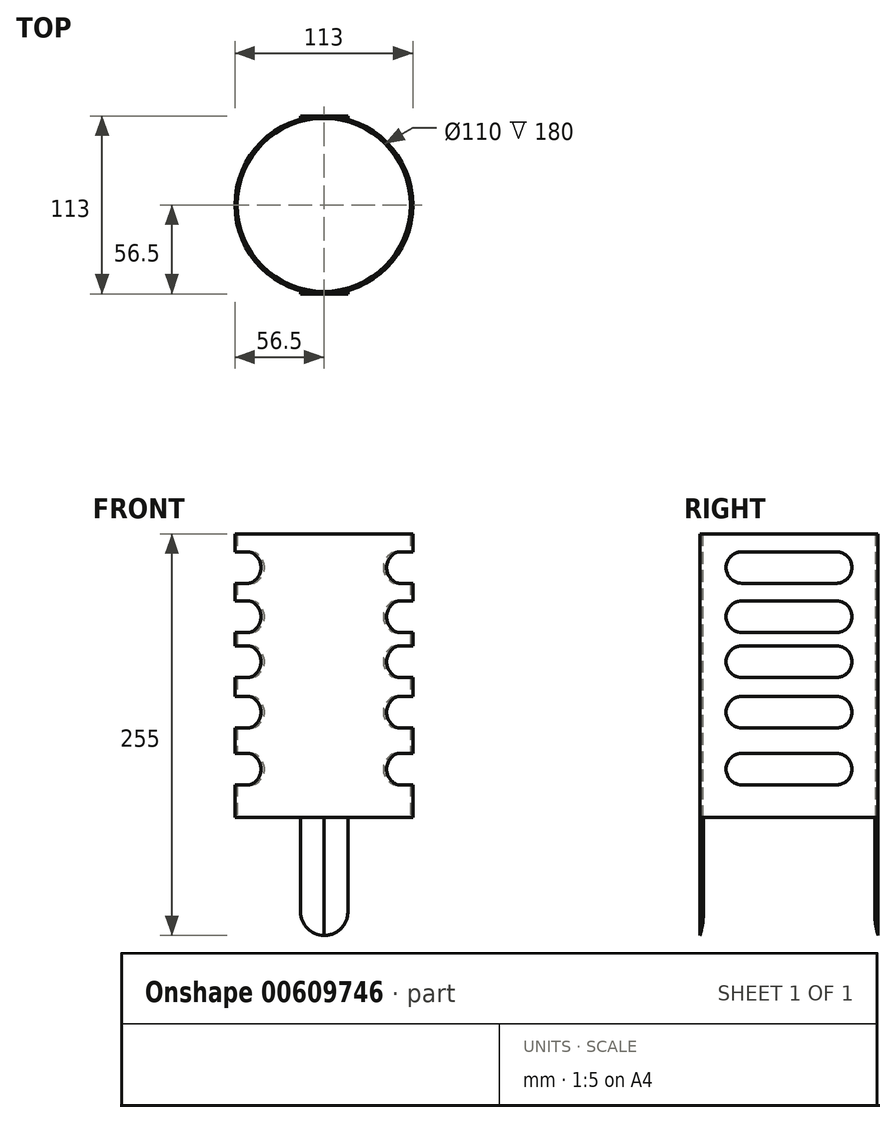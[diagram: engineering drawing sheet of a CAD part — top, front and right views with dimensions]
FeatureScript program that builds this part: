
annotation { "Feature Type Name" : "Feature", "Feature Type Description" : "" }
export const myFeature = defineFeature(function(context is Context, id is Id, definition is map)
    precondition{}
    {
        {
            var Q0;
            Q0=qCreatedBy(makeId("Top.planeOp"),FACE);
            var sketch = newSketch(context, id + "F0", { "sketchPlane" : qUnion([Q0])});
            skCircle(sketch, "E0", {"center": v(0, 0) * mm, "radius": 55 * mm});
            skCircle(sketch, "E1", {"center": v(0, 0) * mm, "radius": 56.5 * mm});
            skSolve(sketch);
        }
        {
            var Q0;
            Q0 = qSketchRegion(id + "F0", true);
            extrude(context, id + "F1", {"entities" : qUnion([Q0]), "depth" : 180 * mm, "offsetDistance" : 25 * mm});
        }
        {
            var Q0;
            Q0=qCreatedBy(makeId("Right.planeOp"),FACE);
            var sketch = newSketch(context, id + "F2", { "sketchPlane" : qUnion([Q0])});
            skLineSegment(sketch, "E2.bottom", {"start": v(-30, 20.7) * mm, "end": v(30, 20.7) * mm});
            skLineSegment(sketch, "E2.top", {"start": v(-30, 40.7) * mm, "end": v(30, 40.7) * mm});
            skLineSegment(sketch, "E2.left", {"start": v(-40, 30.7) * mm, "end": v(-40, 30.7) * mm});
            skLineSegment(sketch, "E2.right", {"start": v(40, 30.7) * mm, "end": v(40, 30.7) * mm});
            skLineSegment(sketch, "E3.bottom", {"start": v(-30, 56.85) * mm, "end": v(30, 56.85) * mm});
            skLineSegment(sketch, "E3.top", {"start": v(-30, 76.85) * mm, "end": v(30, 76.85) * mm});
            skLineSegment(sketch, "E3.left", {"start": v(-40, 66.85) * mm, "end": v(-40, 66.85) * mm});
            skLineSegment(sketch, "E3.right", {"start": v(40, 66.85) * mm, "end": v(40, 66.85) * mm});
            skLineSegment(sketch, "E4.bottom", {"start": v(-30, 88.92) * mm, "end": v(30, 88.92) * mm});
            skLineSegment(sketch, "E4.top", {"start": v(-30, 108.92) * mm, "end": v(30, 108.92) * mm});
            skLineSegment(sketch, "E4.left", {"start": v(-40, 98.92) * mm, "end": v(-40, 98.92) * mm});
            skLineSegment(sketch, "E4.right", {"start": v(40, 98.92) * mm, "end": v(40, 98.92) * mm});
            skLineSegment(sketch, "E5.bottom", {"start": v(-30, 117.47) * mm, "end": v(30, 117.47) * mm});
            skLineSegment(sketch, "E5.top", {"start": v(-30, 137.47) * mm, "end": v(30, 137.47) * mm});
            skLineSegment(sketch, "E5.left", {"start": v(-40, 127.47) * mm, "end": v(-40, 127.47) * mm});
            skLineSegment(sketch, "E5.right", {"start": v(40, 127.47) * mm, "end": v(40, 127.47) * mm});
            skLineSegment(sketch, "E6.bottom", {"start": v(-30, 148.73) * mm, "end": v(30, 148.73) * mm});
            skLineSegment(sketch, "E6.top", {"start": v(-30, 168.73) * mm, "end": v(30, 168.73) * mm});
            skLineSegment(sketch, "E6.left", {"start": v(-40, 158.73) * mm, "end": v(-40, 158.73) * mm});
            skLineSegment(sketch, "E6.right", {"start": v(40, 158.73) * mm, "end": v(40, 158.73) * mm});
            skPoint(sketch, "E7.visualSharp", {"position": v(-40, 168.73) * mm});
            skArc(sketch, "E7.filletArc", {"start": v(-30, 168.73) * mm, "mid": v(-37.07, 165.8) * mm, "end": v(-40, 158.73) * mm});
            skPoint(sketch, "E8.visualSharp", {"position": v(-40, 148.73) * mm});
            skArc(sketch, "E8.filletArc", {"start": v(-40, 158.73) * mm, "mid": v(-37.07, 151.66) * mm, "end": v(-30, 148.73) * mm});
            skPoint(sketch, "E9.visualSharp", {"position": v(-40, 117.47) * mm});
            skArc(sketch, "E9.filletArc", {"start": v(-40, 127.47) * mm, "mid": v(-37.07, 120.4) * mm, "end": v(-30, 117.47) * mm});
            skPoint(sketch, "E10.visualSharp", {"position": v(-40, 108.92) * mm});
            skArc(sketch, "E10.filletArc", {"start": v(-30, 108.92) * mm, "mid": v(-37.07, 106) * mm, "end": v(-40, 98.92) * mm});
            skPoint(sketch, "E11.visualSharp", {"position": v(-40, 88.92) * mm});
            skArc(sketch, "E11.filletArc", {"start": v(-40, 98.92) * mm, "mid": v(-37.07, 91.85) * mm, "end": v(-30, 88.92) * mm});
            skPoint(sketch, "E12.visualSharp", {"position": v(-40, 76.85) * mm});
            skArc(sketch, "E12.filletArc", {"start": v(-30, 76.85) * mm, "mid": v(-37.07, 73.92) * mm, "end": v(-40, 66.85) * mm});
            skPoint(sketch, "E13.visualSharp", {"position": v(-40, 56.85) * mm});
            skArc(sketch, "E13.filletArc", {"start": v(-40, 66.85) * mm, "mid": v(-37.07, 59.78) * mm, "end": v(-30, 56.85) * mm});
            skPoint(sketch, "E14.visualSharp", {"position": v(-40, 40.7) * mm});
            skArc(sketch, "E14.filletArc", {"start": v(-30, 40.7) * mm, "mid": v(-37.07, 37.77) * mm, "end": v(-40, 30.7) * mm});
            skPoint(sketch, "E15.visualSharp", {"position": v(-40, 20.7) * mm});
            skArc(sketch, "E15.filletArc", {"start": v(-40, 30.7) * mm, "mid": v(-37.07, 23.63) * mm, "end": v(-30, 20.7) * mm});
            skPoint(sketch, "E16.visualSharp", {"position": v(40, 20.7) * mm});
            skArc(sketch, "E16.filletArc", {"start": v(30, 20.7) * mm, "mid": v(37.07, 23.63) * mm, "end": v(40, 30.7) * mm});
            skPoint(sketch, "E17.visualSharp", {"position": v(40, 40.7) * mm});
            skArc(sketch, "E17.filletArc", {"start": v(40, 30.7) * mm, "mid": v(37.07, 37.77) * mm, "end": v(30, 40.7) * mm});
            skPoint(sketch, "E18.visualSharp", {"position": v(40, 56.85) * mm});
            skArc(sketch, "E18.filletArc", {"start": v(30, 56.85) * mm, "mid": v(37.07, 59.78) * mm, "end": v(40, 66.85) * mm});
            skPoint(sketch, "E19.visualSharp", {"position": v(40, 88.92) * mm});
            skArc(sketch, "E19.filletArc", {"start": v(30, 88.92) * mm, "mid": v(37.07, 91.85) * mm, "end": v(40, 98.92) * mm});
            skPoint(sketch, "E20.visualSharp", {"position": v(40, 76.85) * mm});
            skArc(sketch, "E20.filletArc", {"start": v(40, 66.85) * mm, "mid": v(37.07, 73.92) * mm, "end": v(30, 76.85) * mm});
            skPoint(sketch, "E21.visualSharp", {"position": v(40, 108.92) * mm});
            skArc(sketch, "E21.filletArc", {"start": v(40, 98.92) * mm, "mid": v(37.07, 106) * mm, "end": v(30, 108.92) * mm});
            skPoint(sketch, "E22.visualSharp", {"position": v(40, 137.47) * mm});
            skArc(sketch, "E22.filletArc", {"start": v(40, 127.47) * mm, "mid": v(37.07, 134.54) * mm, "end": v(30, 137.47) * mm});
            skPoint(sketch, "E23.visualSharp", {"position": v(40, 168.73) * mm});
            skArc(sketch, "E23.filletArc", {"start": v(40, 158.73) * mm, "mid": v(37.07, 165.8) * mm, "end": v(30, 168.73) * mm});
            skPoint(sketch, "E24.visualSharp", {"position": v(40, 148.73) * mm});
            skArc(sketch, "E24.filletArc", {"start": v(30, 148.73) * mm, "mid": v(37.07, 151.66) * mm, "end": v(40, 158.73) * mm});
            skPoint(sketch, "E25.visualSharp", {"position": v(40, 117.47) * mm});
            skArc(sketch, "E25.filletArc", {"start": v(30, 117.47) * mm, "mid": v(37.07, 120.4) * mm, "end": v(40, 127.47) * mm});
            skPoint(sketch, "E26.visualSharp", {"position": v(-40, 137.47) * mm});
            skArc(sketch, "E26.filletArc", {"start": v(-30, 137.47) * mm, "mid": v(-37.07, 134.54) * mm, "end": v(-40, 127.47) * mm});
            skSolve(sketch);
        }
        {
            var Q0;
            Q0 = qSketchRegion(id + "F2", true);
            extrude(context, id + "F3", {"entities" : qUnion([Q0]), "operationType" : NewBodyOperationType.REMOVE, "endBound" : BoundingType.SYMMETRIC, "depth" : 150 * mm, "offsetDistance" : 25 * mm});
        }
        {
            var Q0;
            Q0=qCreatedBy(makeId("Front.planeOp"),FACE);
            var sketch = newSketch(context, id + "F4", { "sketchPlane" : qUnion([Q0])});
            skLineSegment(sketch, "E27.bottom", {"start": v(-14.73, 0) * mm, "end": v(15.27, 0) * mm});
            skLineSegment(sketch, "E27.top", {"start": v(-14.73, -60) * mm, "end": v(15.27, -60) * mm});
            skLineSegment(sketch, "E27.left", {"start": v(-14.73, 0) * mm, "end": v(-14.73, -60) * mm});
            skLineSegment(sketch, "E27.right", {"start": v(15.27, 0) * mm, "end": v(15.27, -60) * mm});
            skArc(sketch, "E28", {"start": v(-14.73, -60) * mm, "mid": v(0.27, -75) * mm, "end": v(15.27, -60) * mm});
            skSolve(sketch);
        }
        {
            var Q0;
            Q0 = qSketchRegion(id + "F4", true);
            extrude(context, id + "F5", {"entities" : qUnion([Q0]), "operationType" : NewBodyOperationType.ADD, "endBound" : BoundingType.SYMMETRIC, "depth" : 113 * mm, "offsetDistance" : 25 * mm});
        }
        {
            var Q0;
            Q0=qCreatedBy(makeId("Top.planeOp"),FACE);
            var sketch = newSketch(context, id + "F6", { "sketchPlane" : qUnion([Q0])});
            skCircle(sketch, "E29", {"center": v(0, 0) * mm, "radius": 55 * mm});
            skSolve(sketch);
        }
        {
            var Q0;
            Q0 = qSketchRegion(id + "F6", true);
            extrude(context, id + "F7", {"entities" : qUnion([Q0]), "operationType" : NewBodyOperationType.REMOVE, "oppositeDirection" : true, "depth" : 110 * mm, "offsetDistance" : 25 * mm});
        }
        {
            var Q0;
            Q0=qCreatedBy(makeId("Top.planeOp"),FACE);
            var sketch = newSketch(context, id + "F8", { "sketchPlane" : qUnion([Q0])});
            skCircle(sketch, "E30", {"center": v(0, 0) * mm, "radius": 56.5 * mm});
            skSolve(sketch);
        }
        {
            var Q0;
            Q0 = qSketchRegion(id + "F8", true);
            extrude(context, id + "F9", {"entities" : qUnion([Q0]), "operationType" : NewBodyOperationType.REMOVE, "oppositeDirection" : true, "depth" : 164.8 * mm, "offsetDistance" : 25 * mm});
        }
    });
